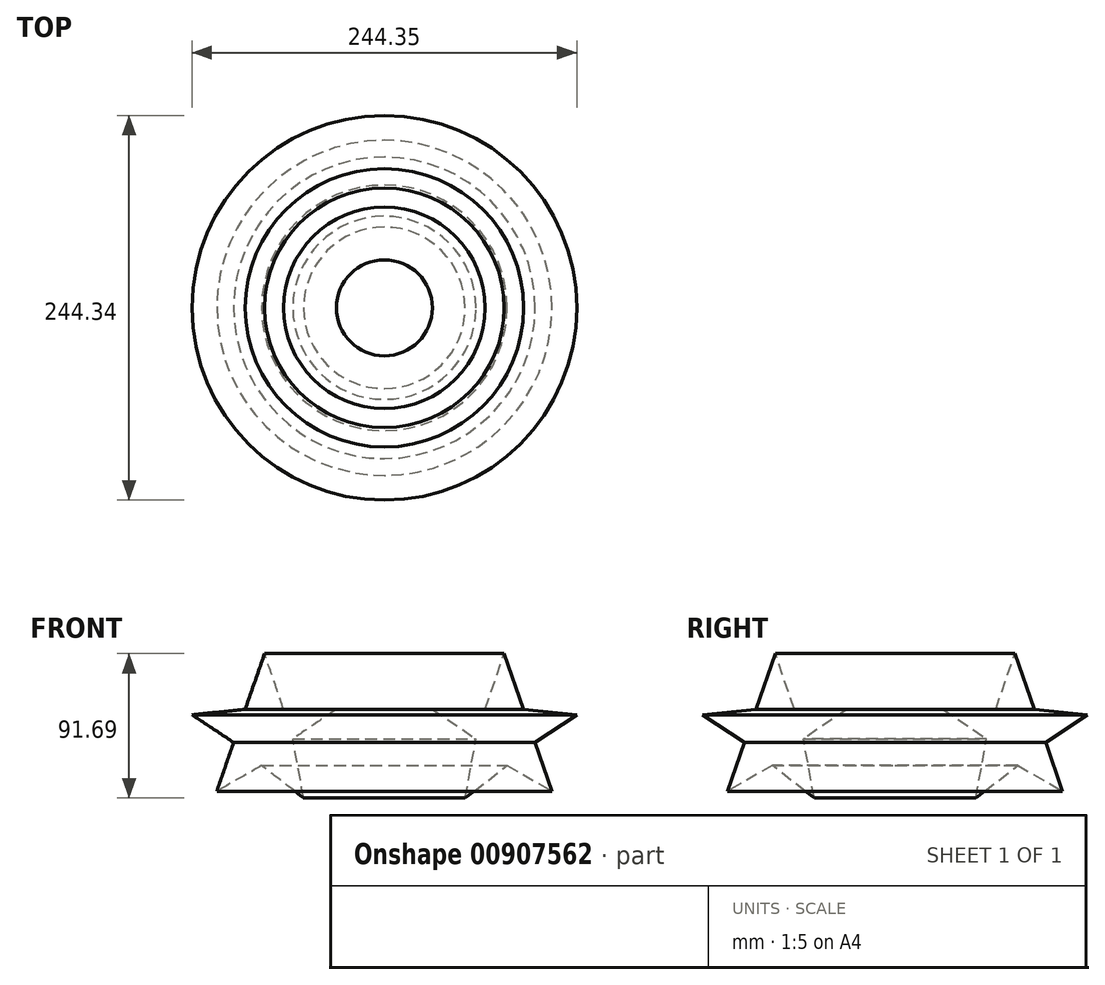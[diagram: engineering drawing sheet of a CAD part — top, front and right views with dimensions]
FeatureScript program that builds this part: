
annotation { "Feature Type Name" : "Feature", "Feature Type Description" : "" }
export const myFeature = defineFeature(function(context is Context, id is Id, definition is map)
    precondition{}
    {
        {
            var Q0;
            Q0=qCreatedBy(makeId("Front.planeOp"),FACE);
            var sketch = newSketch(context, id + "F0", { "sketchPlane" : qUnion([Q0])});
            skLineSegment(sketch, "E0", {"start": v(-12.06, 23.5) * mm, "end": v(0, 58.8) * mm});
            skLineSegment(sketch, "E1", {"start": v(0, 58.8) * mm, "end": v(12.32, 23.5) * mm});
            skLineSegment(sketch, "E2", {"start": v(-12.06, 23.5) * mm, "end": v(-45.6, 23.5) * mm});
            skLineSegment(sketch, "E3", {"start": v(-45.6, 23.5) * mm, "end": v(-17.9, 4.7) * mm});
            skLineSegment(sketch, "E4", {"start": v(-17.9, 4.7) * mm, "end": v(-24.76, -32.9) * mm});
            skLineSegment(sketch, "E5", {"start": v(12.32, 23.5) * mm, "end": v(46.1, 19.94) * mm});
            skLineSegment(sketch, "E6", {"start": v(46.1, 19.94) * mm, "end": v(19.69, 2.41) * mm});
            skLineSegment(sketch, "E7", {"start": v(-24.76, -32.9) * mm, "end": v(1.9, -12.32) * mm});
            skLineSegment(sketch, "E8", {"start": v(1.9, -12.32) * mm, "end": v(30.35, -28.58) * mm});
            skLineSegment(sketch, "E9", {"start": v(19.69, 2.41) * mm, "end": v(30.35, -28.58) * mm});
            skSolve(sketch);
        }
        {
            var Q0;
            Q0=qCreatedBy(makeId("Front.planeOp"),FACE);
            var sketch = newSketch(context, id + "F1", { "sketchPlane" : qUnion([Q0])});
            skLineSegment(sketch, "E10", {"start": v(-76.07, 0) * mm, "end": v(-76.07, 68.2) * mm});
            skSolve(sketch);
        }
        {
            var Q0;
            Q0=makeQuery(id+"F0.imprint","IMPRINT",FACE,{"disambiguationData":[TD([[makeQuery(id+"F0.imprint","IMPRINT",EDGE,{"derivedFrom":sQuery(id+"F0.wireOp",EDGE,"E0")}),-1.0]])]});
            var Q1;
            Q1=sQuery(id+"F1.wireOp",EDGE,"E10");
            revolve(context, id + "F2", {"surfaceOperationType" : NewSurfaceOperationType.NEW, "entities" : qUnion([Q0]), "axis" : qUnion([Q1]), "revolveType" : RevolveType.FULL});
        }
    });
